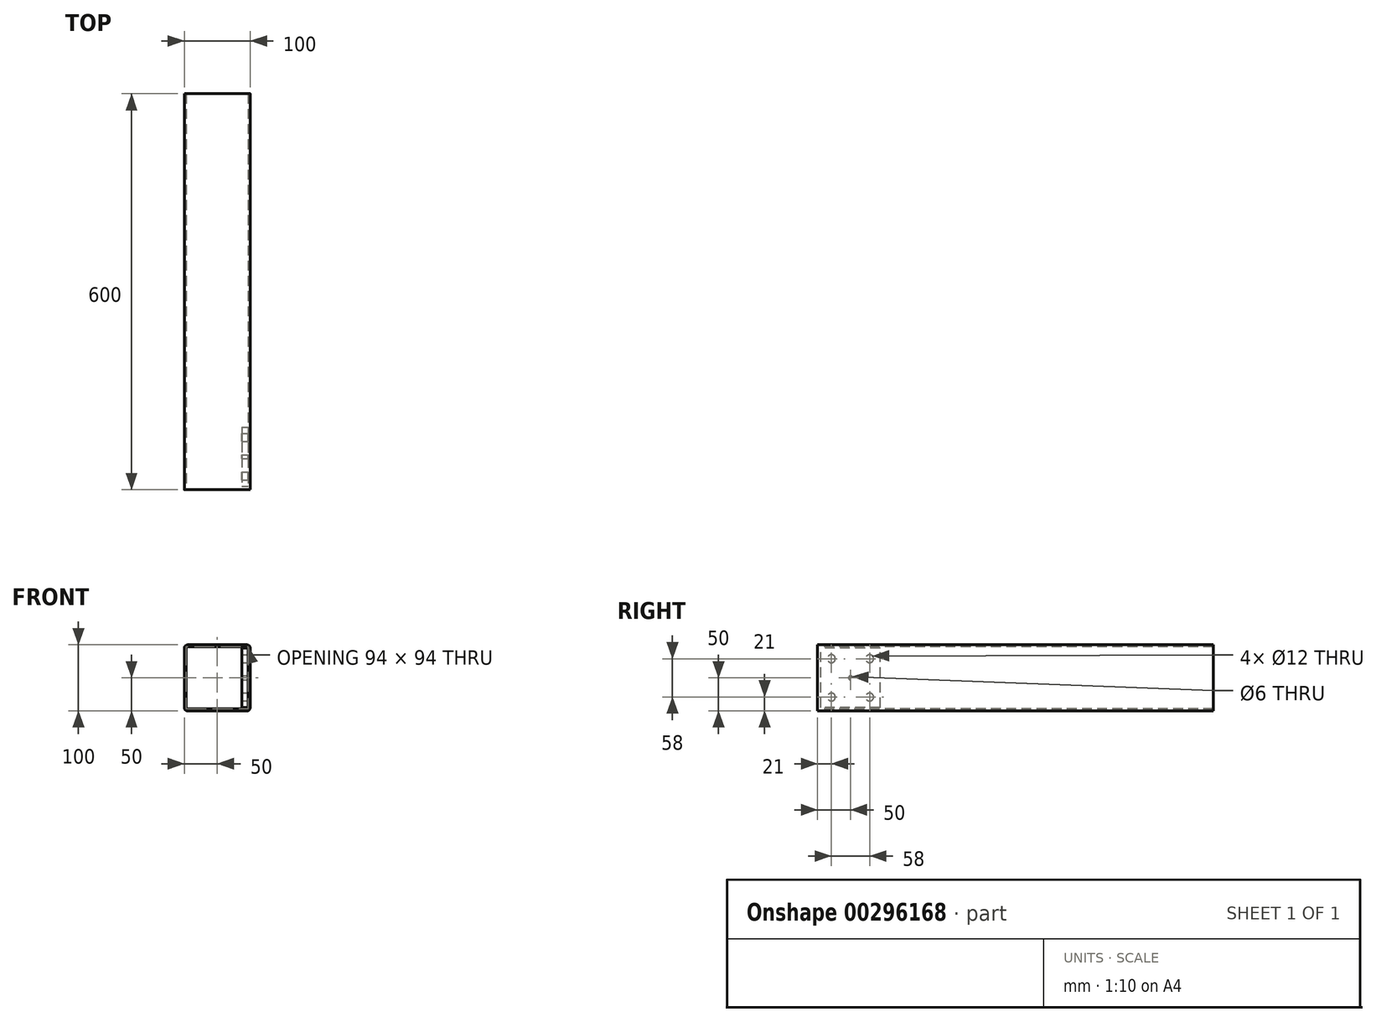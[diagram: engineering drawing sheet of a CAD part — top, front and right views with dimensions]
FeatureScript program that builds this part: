
annotation { "Feature Type Name" : "Feature", "Feature Type Description" : "" }
export const myFeature = defineFeature(function(context is Context, id is Id, definition is map)
    precondition{}
    {
        {
            var Q0;
            Q0=qCreatedBy(makeId("Front.planeOp"),FACE);
            var sketch = newSketch(context, id + "F0", { "sketchPlane" : qUnion([Q0])});
            skLineSegment(sketch, "E0.bottom", {"start": v(45, 50) * mm, "end": v(-45, 50) * mm});
            skLineSegment(sketch, "E0.top", {"start": v(45, -50) * mm, "end": v(-45, -50) * mm});
            skLineSegment(sketch, "E0.left", {"start": v(50, 45) * mm, "end": v(50, -45) * mm});
            skLineSegment(sketch, "E0.right", {"start": v(-50, 45) * mm, "end": v(-50, -45) * mm});
            skPoint(sketch, "E0.middle", {"position": v(0, 0) * mm});
            skPoint(sketch, "E1.visualSharp", {"position": v(-50, 50) * mm});
            skArc(sketch, "E1.filletArc", {"start": v(-45, 50) * mm, "mid": v(-48.54, 48.54) * mm, "end": v(-50, 45) * mm});
            skPoint(sketch, "E2.visualSharp", {"position": v(50, 50) * mm});
            skArc(sketch, "E2.filletArc", {"start": v(50, 45) * mm, "mid": v(48.54, 48.54) * mm, "end": v(45, 50) * mm});
            skPoint(sketch, "E3.visualSharp", {"position": v(50, -50) * mm});
            skArc(sketch, "E3.filletArc", {"start": v(45, -50) * mm, "mid": v(48.54, -48.54) * mm, "end": v(50, -45) * mm});
            skPoint(sketch, "E4.visualSharp", {"position": v(-50, -50) * mm});
            skArc(sketch, "E4.filletArc", {"start": v(-50, -45) * mm, "mid": v(-48.54, -48.54) * mm, "end": v(-45, -50) * mm});
            skArc(sketch, "E5.0", {"start": v(-45, 47) * mm, "mid": v(-46.41, 46.41) * mm, "end": v(-47, 45) * mm});
            skLineSegment(sketch, "E5.1", {"start": v(45, 47) * mm, "end": v(-45, 47) * mm});
            skLineSegment(sketch, "E5.2", {"start": v(-47, 45) * mm, "end": v(-47, -45) * mm});
            skArc(sketch, "E5.3", {"start": v(47, 45) * mm, "mid": v(46.41, 46.41) * mm, "end": v(45, 47) * mm});
            skArc(sketch, "E5.4", {"start": v(-47, -45) * mm, "mid": v(-46.41, -46.41) * mm, "end": v(-45, -47) * mm});
            skLineSegment(sketch, "E5.5", {"start": v(45, -47) * mm, "end": v(-45, -47) * mm});
            skArc(sketch, "E5.6", {"start": v(45, -47) * mm, "mid": v(46.41, -46.41) * mm, "end": v(47, -45) * mm});
            skLineSegment(sketch, "E5.7", {"start": v(47, 45) * mm, "end": v(47, -45) * mm});
            skSolve(sketch);
        }
        {
            var Q0;
            Q0=makeQuery(id+"F0.imprint","IMPRINT",FACE,{"disambiguationData":[TD([[makeQuery(id+"F0.imprint","IMPRINT",EDGE,{"derivedFrom":sQuery(id+"F0.wireOp",EDGE,"E0.bottom")}),1.0]])]});
            extrude(context, id + "F1", {"entities" : qUnion([Q0]), "oppositeDirection" : true, "depth" : 600 * mm});
        }
        {
            var Q0;
            Q0=makeQuery(id+"F1.opExtrude","SWEPT_FACE",FACE,{"disambiguationData":[OSD([sQuery(id+"F0.wireOp",EDGE,"E5.7")])]});
            var sketch = newSketch(context, id + "F2", { "sketchPlane" : qUnion([Q0])});
            skLineSegment(sketch, "E6.bottom", {"start": v(-95, -45) * mm, "end": v(-5, -45) * mm});
            skLineSegment(sketch, "E6.top", {"start": v(-95, 45) * mm, "end": v(-5, 45) * mm});
            skLineSegment(sketch, "E6.left", {"start": v(-95, -45) * mm, "end": v(-95, 45) * mm});
            skLineSegment(sketch, "E6.right", {"start": v(-5, -45) * mm, "end": v(-5, 45) * mm});
            skPoint(sketch, "E6.middle", {"position": v(-50, 0) * mm});
            skLineSegment(sketch, "E7", {"start": v(-5, 45) * mm, "end": v(-95, -45) * mm, "construction": true});
            skLineSegment(sketch, "E8", {"start": v(-95, 45) * mm, "end": v(-5, -45) * mm, "construction": true});
            skLineSegment(sketch, "E9", {"start": v(-5, -29) * mm, "end": v(-95, -29) * mm, "construction": true});
            skCircle(sketch, "E10", {"center": v(-79, -29) * mm, "radius": 6 * mm});
            skCircle(sketch, "E11", {"center": v(-21, -29) * mm, "radius": 6 * mm});
            skLineSegment(sketch, "E12", {"start": v(-21, -29) * mm, "end": v(-21, 29) * mm, "construction": true});
            skLineSegment(sketch, "E13", {"start": v(-21, 29) * mm, "end": v(-79, 29) * mm, "construction": true});
            skCircle(sketch, "E14", {"center": v(-79, 29) * mm, "radius": 6 * mm});
            skCircle(sketch, "E15", {"center": v(-21, 29) * mm, "radius": 6 * mm});
            skCircle(sketch, "E16", {"center": v(-50, 0) * mm, "radius": 3 * mm});
            skSolve(sketch);
        }
        {
            var Q0;
            Q0 = qSketchRegion(id + "F2", true);
            extrude(context, id + "F3", {"entities" : qUnion([Q0]), "depth" : 10 * mm});
        }
    });
